# Revit family: MTXTYP005
name_source: partatom
category: Furniture
units: mm (PartAtom-declared; Revit-internal decimal feet)

## family parameters
Always vertical = Yes
Cut with Voids When Loaded = No
OmniClass Number = 23.40.20.00
OmniClass Title = General Furniture and Specialties
Render Appearance Source = Family Geometry
Room Calculation Point = No
Shared = No
Work Plane-Based = No

## types (1)
- MTXTYP005
    Cost = 39745 $
    Default Elevation = 0 mm  [stored 0 ft]
    Description = 1 x Wall Mounted Open Overhead - 08Hx78Wx14D, 4 x Matrix Black Duplex Outlet - Line 1, 4 x Matrix Black Duplex Outlet - Line 2, 3 x 18 in. Electrical Jumper  (Panel To Panel), 2 x Single Powerway Assembly - 42W - 8 wire, 4 circuit, 2 x Double Powerway Assembly - 36W - 8 wire, 4 circuit, 2 x Access Hole Cover, 1 x LH Receptacle Mounted Base Infeed - 72L - 8 Wire, 4 Circuit, 2 x Universal 8 Wire 4 Cir I Connector, 2 x 24 in. Electrical Jumper  (Vt 24), 2 x Dual Electrical Tile - 8H X 36W, 1 x Dual Electrical Tile - 8H X 36W, 2 x Dual Electrical Tile - 8H X 42W, 6 x Tackable Acoustical Tile - 16H x 36W, 2 x Tackable Acoustical Tile - 32H x 42W, 1 x Tackable Acoustical Tile - 40H x 36W, 2 x Tackable Acoustical Tile - 40H x 42W, 2 x Panel Frame - Linear Trim - 42H x 36W, 2 x Panel Frame - Linear Trim - 42H x 42W, 1 x MTX Gallery Panel EOR DBL-42H x 60W Horz, 1 x MTX Gallery Panel EOR Single-42H x 30W LH Horz, 1 x MATRIX RECESSED FRAMELESS GLASS 8"H X 36"W V2, 1 x MATRIX RECESSED FRAMELESS GLASS 8"H X 42"W V2, 1 x Matrix Linear Single Frame Recessed Glass Top Cap Kit 36", 1 x Matrix Linear Single Frame Recessed Glass Top Cap Kit 42", 2 x Rectangular - 2mm Edge - 24D x 78W, 2 x Rectangular - 2mm Edge - 30D x 48W, 2 x Rectangular - 2mm Edge - 36D x 72W, 6 x Post Leg 2.5 x 2.5 27H, 7 x Flat Plate, 3 x Side/Support Rear Bracket - Left, 1 x Side/Support Rear Bracket - Right, 2 x Regular Cantilever - Left Hand - 24D, 1 x Shared Cantilever - Single - 24D, 2 x U-Channel - 48W, 1 x Cbx Full Depth Lat Bbf 18dx28hx30w, 1 x Cbx Full Depth Lat Bbf 24dx28hx30w, 2 x Cbx Full Depth Floor Bookcase 18dx21hx36w, 1 x Cbx 2d Full Depth Cab 18dx21hx42w, 1 x Cbx Full Depth Lat Bf 18dx21hx42w
    Exported From CET Designer = Yes
    Manufacturer = AIS
    Model = C-OWM087814
    Show MTXTYP005 = Yes
    VisibilityIndex = 0

note: [stored X ft] marks values corroborated as IEEE doubles in the binary element streams (Revit-internal decimal feet)

## geometry (parser evidence)
native form markers: Sweep x3
no freeform markers — native parametric forms only
